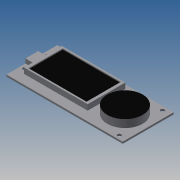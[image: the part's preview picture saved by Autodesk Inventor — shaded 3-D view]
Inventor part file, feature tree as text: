
AUTODESK INVENTOR PART (.ipt)
format: ipt  version: 2013 (Build 170138000, 138)  size: 157,696 bytes
history: native  units: mm
features: extrude x7, sketch x7
ambient origin geometry x8: Origin, YZ Plane, XZ Plane, XY Plane, X Axis, Y Axis, Z Axis, Center Point
bodies: Solid1 (feature_tree)
feature tree (14):
  extrude  "Extrusion1"  Depth=46.0mm
  extrude  "Extrusion2"  Depth=57.5mm
  extrude  "Extrusion3"  Depth=32.0mm
  extrude  "Extrusion4"  Depth=23.0mm
  extrude  "Extrusion5"  Depth=3.5mm
  extrude  "Extrusion6"  Depth=2.0mm TaperAngle=0.0deg
  extrude  "Extrusion7"  Depth=1.0mm TaperAngle=0.0deg
  sketch  "Sketch1"  dims[d0=105.2mm d2=46.0mm]
  sketch  "Sketch2"  dims[d3=1.6mm d4=0.0mm d5=57.5mm]
  sketch  "Sketch3"  dims[d7=34.0mm d8=32.0mm]
  sketch  "Sketch4"  dims[d9=21.0mm d10=23.0mm]
  sketch  "Sketch5"  dims[d11=7.0mm d12=0.0mm d13=3.5mm]
  sketch  "Sketch6"  dims[d14=7.5mm d15=2.0mm d16=0.0mm]
  sketch  "Sketch7"  dims[d21=60.96mm d22=1.0mm d23=0.0mm d24=11.5mm d26=4.0mm d27=0.0mm d28=2.5mm d29=0.2mm d30=0.2mm d31=0.2mm d32=4.0mm d33=0.0mm d34=20.25mm d36=3.75mm d37=39.0mm d39=6.5mm d40=3.5mm d41=4.0mm d42=0.0mm]
